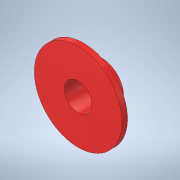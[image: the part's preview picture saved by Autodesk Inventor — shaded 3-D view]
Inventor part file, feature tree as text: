
AUTODESK INVENTOR PART (.ipt)
format: ipt  version: 2021 (Build 250183000, 183)  size: 113,664 bytes
history: native  units: in
note: dims shown in document units (in); Inventor stores cm internally (conversion verified against a paired STEP export)
features: sketch x2, revolve x1, extrude x1
ambient origin geometry x8: Origin, YZ Plane, XZ Plane, XY Plane, X Axis, Y Axis, Z Axis, Center Point
bodies: Solid1 (feature_tree)
feature tree (4):
  revolve  "Revolution1"  [1 undecoded]
  extrude  "Extrusion1"  Depth=0.259in
  sketch  "Sketch1"  dims[d0=0.625in d1=0.0787in]
  sketch  "Sketch2"  dims[d2=0.315in d3=0.259in d4=90.0deg d5=0.394in d6=1.0in d7=0.0in]
note: 1 required parameter value undecoded (feature->parameter linkage not recoverable at this tier; creation-order binding heuristic only, values carry confidence <= 0.55)
